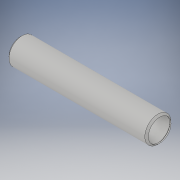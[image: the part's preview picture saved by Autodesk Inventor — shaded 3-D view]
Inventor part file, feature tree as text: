
AUTODESK INVENTOR PART (.ipt)
format: ipt  version: 2019 (Build 230136000, 136)  size: 123,904 bytes
history: native  units: mm
features: other x14, revolve x1, sketch x1
ambient origin geometry x8: Origin, YZ Plane, XZ Plane, XY Plane, X Axis, Y Axis, Z Axis, Center Point
bodies: Solid1 (feature_tree)
feature tree (16):
  revolve  "Revolution1"  [1 undecoded]
  other  "cap_XY"
  other  "cap_YZ"
  other  "cap_ZX"
  other  "cap_X"
  other  "cap_Y"
  other  "cap_Z"
  other  "cap_Center"
  other  "head_XY"
  other  "head_YZ"
  other  "head_ZX"
  other  "head_X"
  other  "head_Y"
  other  "head_Z"
  other  "head_Center"
  sketch  "Sketch_1"  dims[d0=360.0deg]
note: 1 required parameter value undecoded (feature->parameter linkage not recoverable at this tier; creation-order binding heuristic only, values carry confidence <= 0.55)
